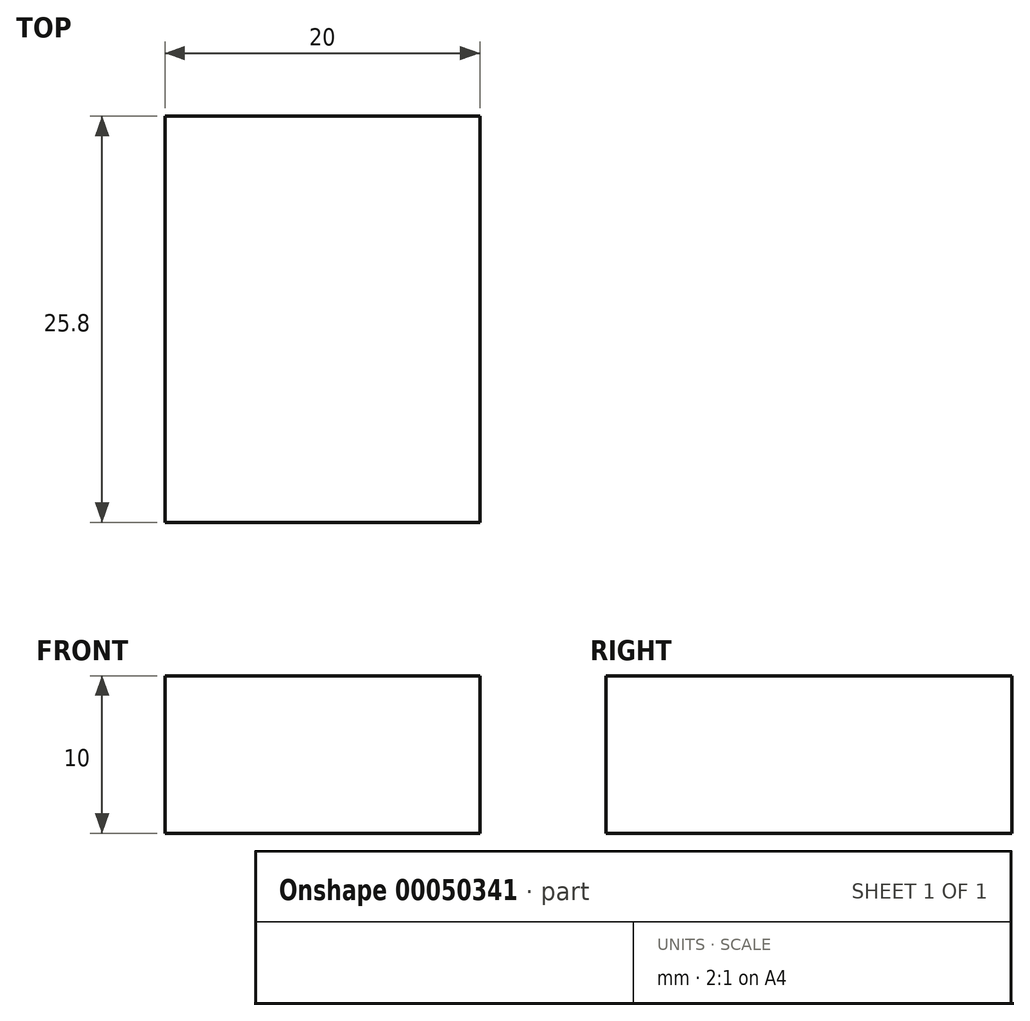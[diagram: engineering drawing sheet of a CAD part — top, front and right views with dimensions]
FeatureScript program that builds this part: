
annotation { "Feature Type Name" : "Feature", "Feature Type Description" : "" }
export const myFeature = defineFeature(function(context is Context, id is Id, definition is map)
    precondition{}
    {
        {
            var Q0;
            Q0=qCreatedBy(makeId("Front.planeOp"),FACE);
            var sketch = newSketch(context, id + "F0", { "sketchPlane" : qUnion([Q0])});
            skLineSegment(sketch, "E0.bottom", {"start": v(0, 0) * mm, "end": v(20, 0) * mm});
            skLineSegment(sketch, "E0.top", {"start": v(0, -10) * mm, "end": v(20, -10) * mm});
            skLineSegment(sketch, "E0.left", {"start": v(0, 0) * mm, "end": v(0, -10) * mm});
            skLineSegment(sketch, "E0.right", {"start": v(20, 0) * mm, "end": v(20, -10) * mm});
            skSolve(sketch);
        }
        {
            var Q0;
            Q0=makeQuery(id+"F0.imprint","IMPRINT",FACE,{"disambiguationData":[TD([[makeQuery(id+"F0.imprint","IMPRINT",EDGE,{"derivedFrom":sQuery(id+"F0.wireOp",EDGE,"E0.bottom")}),-1.0]])]});
            extrude(context, id + "F1", {"entities" : qUnion([Q0]), "depth" : 25.8 * mm});
        }
    });
